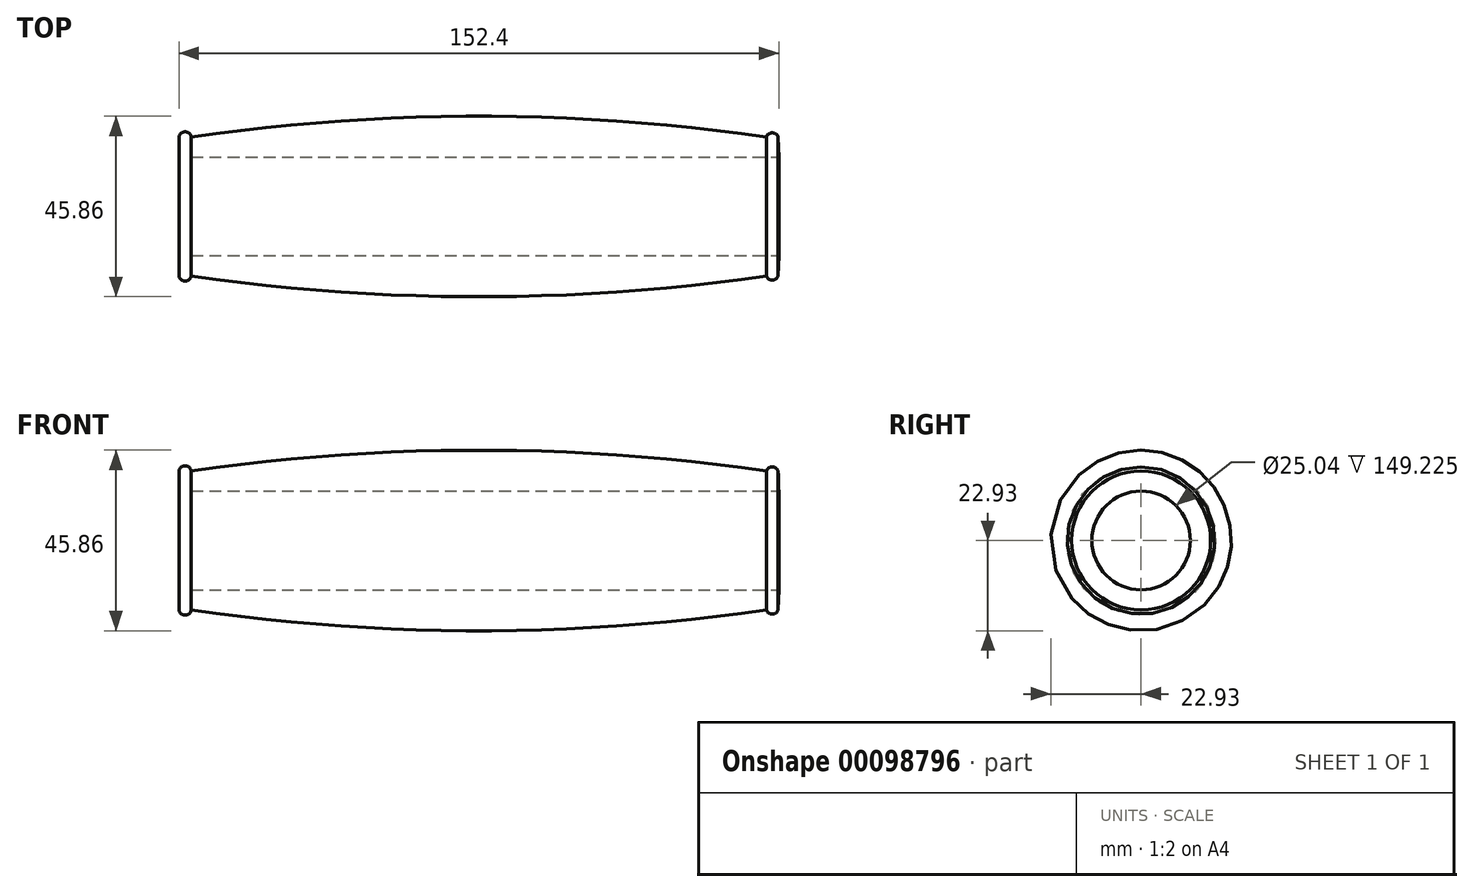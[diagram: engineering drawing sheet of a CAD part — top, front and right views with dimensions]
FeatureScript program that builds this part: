
annotation { "Feature Type Name" : "Feature", "Feature Type Description" : "" }
export const myFeature = defineFeature(function(context is Context, id is Id, definition is map)
    precondition{}
    {
        {
            var Q0;
            Q0=qCreatedBy(makeId("Front.planeOp"),FACE);
            var sketch = newSketch(context, id + "F0", { "sketchPlane" : qUnion([Q0])});
            skLineSegment(sketch, "E0", {"start": v(3.17, 12.52) * mm, "end": v(152.4, 12.52) * mm});
            skLineSegment(sketch, "E1", {"start": v(3.18, 0) * mm, "end": v(3.17, 12.52) * mm});
            skArc(sketch, "E2", {"start": v(149.22, 17.66) * mm, "mid": v(76.19, 22.93) * mm, "end": v(3.15, 17.65) * mm});
            skArc(sketch, "E3", {"start": v(3.15, 17.65) * mm, "mid": v(1.57, 18.97) * mm, "end": v(0, 17.65) * mm});
            skArc(sketch, "E4", {"start": v(152.24, 17.66) * mm, "mid": v(150.73, 18.72) * mm, "end": v(149.23, 17.66) * mm});
            skPoint(sketch, "E5.orphan", {"position": v(0, 12.52) * mm});
            skLineSegment(sketch, "E6", {"start": v(3.18, 0) * mm, "end": v(0, 0) * mm});
            skLineSegment(sketch, "E7", {"start": v(0, 0) * mm, "end": v(0, 17.65) * mm});
            skLineSegment(sketch, "E8", {"start": v(152.4, 12.52) * mm, "end": v(152.24, 17.66) * mm});
            skSolve(sketch);
        }
        {
            var Q0;
            Q0=qCreatedBy(makeId("Right.planeOp"),FACE);
            var sketch = newSketch(context, id + "F1", { "sketchPlane" : qUnion([Q0])});
            skCircle(sketch, "E9", {"center": v(0, 0) * mm, "radius": 12.63 * mm});
            skSolve(sketch);
        }
        {
            var Q0;
            Q0=makeQuery(id+"F0.imprint","IMPRINT",FACE,{"disambiguationData":[TD([[makeQuery(id+"F0.imprint","IMPRINT",EDGE,{"derivedFrom":sQuery(id+"F0.wireOp",EDGE,"E0")}),1.0]])]});
            var Q1;
            Q1=sQuery(id+"F1.wireOp",EDGE,"E9");
            sweep(context, id + "F2", {"profiles" : qUnion([Q0]), "path" : qUnion([Q1])});
        }
    });
